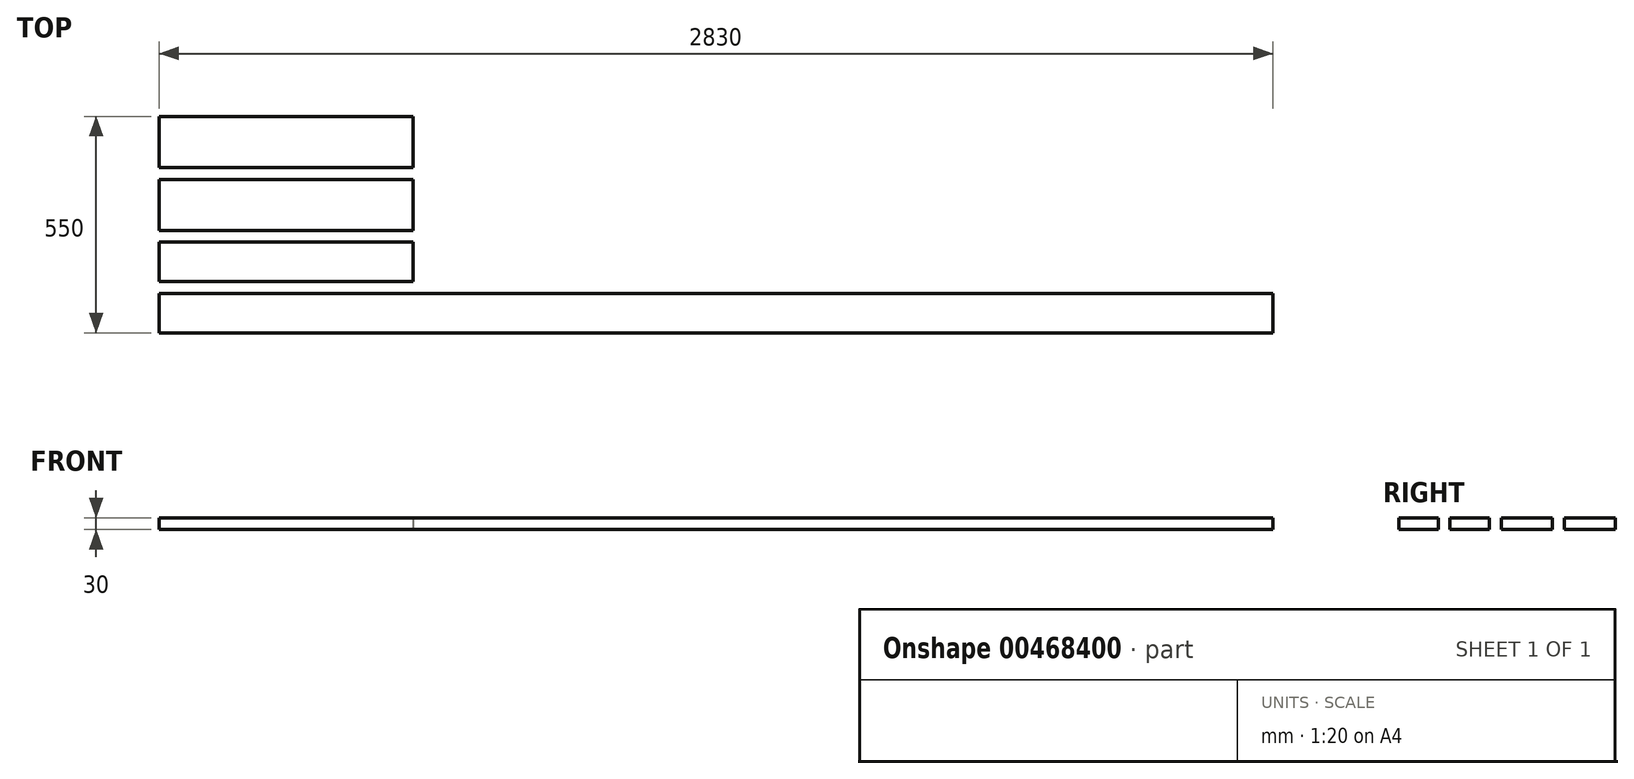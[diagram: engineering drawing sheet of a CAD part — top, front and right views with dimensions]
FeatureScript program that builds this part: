
annotation { "Feature Type Name" : "Feature", "Feature Type Description" : "" }
export const myFeature = defineFeature(function(context is Context, id is Id, definition is map)
    precondition{}
    {
        {
            var Q0;
            Q0=qCreatedBy(makeId("Top.planeOp"),FACE);
            var sketch = newSketch(context, id + "F0", { "sketchPlane" : qUnion([Q0])});
            skLineSegment(sketch, "E0.bottom", {"start": v(0, 0) * mm, "end": v(645, 0) * mm});
            skLineSegment(sketch, "E0.top", {"start": v(0, 130) * mm, "end": v(645, 130) * mm});
            skLineSegment(sketch, "E0.left", {"start": v(0, 0) * mm, "end": v(0, 130) * mm});
            skLineSegment(sketch, "E0.right", {"start": v(645, 0) * mm, "end": v(645, 130) * mm});
            skLineSegment(sketch, "E1.bottom", {"start": v(0, -30) * mm, "end": v(645, -30) * mm});
            skLineSegment(sketch, "E1.top", {"start": v(0, -160) * mm, "end": v(645, -160) * mm});
            skLineSegment(sketch, "E1.left", {"start": v(0, -30) * mm, "end": v(0, -160) * mm});
            skLineSegment(sketch, "E1.right", {"start": v(645, -30) * mm, "end": v(645, -160) * mm});
            skLineSegment(sketch, "E2.bottom", {"start": v(0, -190) * mm, "end": v(645, -190) * mm});
            skLineSegment(sketch, "E2.top", {"start": v(0, -290) * mm, "end": v(645, -290) * mm});
            skLineSegment(sketch, "E2.left", {"start": v(0, -190) * mm, "end": v(0, -290) * mm});
            skLineSegment(sketch, "E2.right", {"start": v(645, -190) * mm, "end": v(645, -290) * mm});
            skLineSegment(sketch, "E3.bottom", {"start": v(0, -320) * mm, "end": v(2830, -320) * mm});
            skLineSegment(sketch, "E3.top", {"start": v(0, -420) * mm, "end": v(2830, -420) * mm});
            skLineSegment(sketch, "E3.left", {"start": v(0, -320) * mm, "end": v(0, -420) * mm});
            skLineSegment(sketch, "E3.right", {"start": v(2830, -320) * mm, "end": v(2830, -420) * mm});
            skSolve(sketch);
        }
        {
            var Q0;
            Q0 = qSketchRegion(id + "F0", true);
            extrude(context, id + "F1", {"entities" : qUnion([Q0]), "depth" : 30 * mm});
        }
    });
